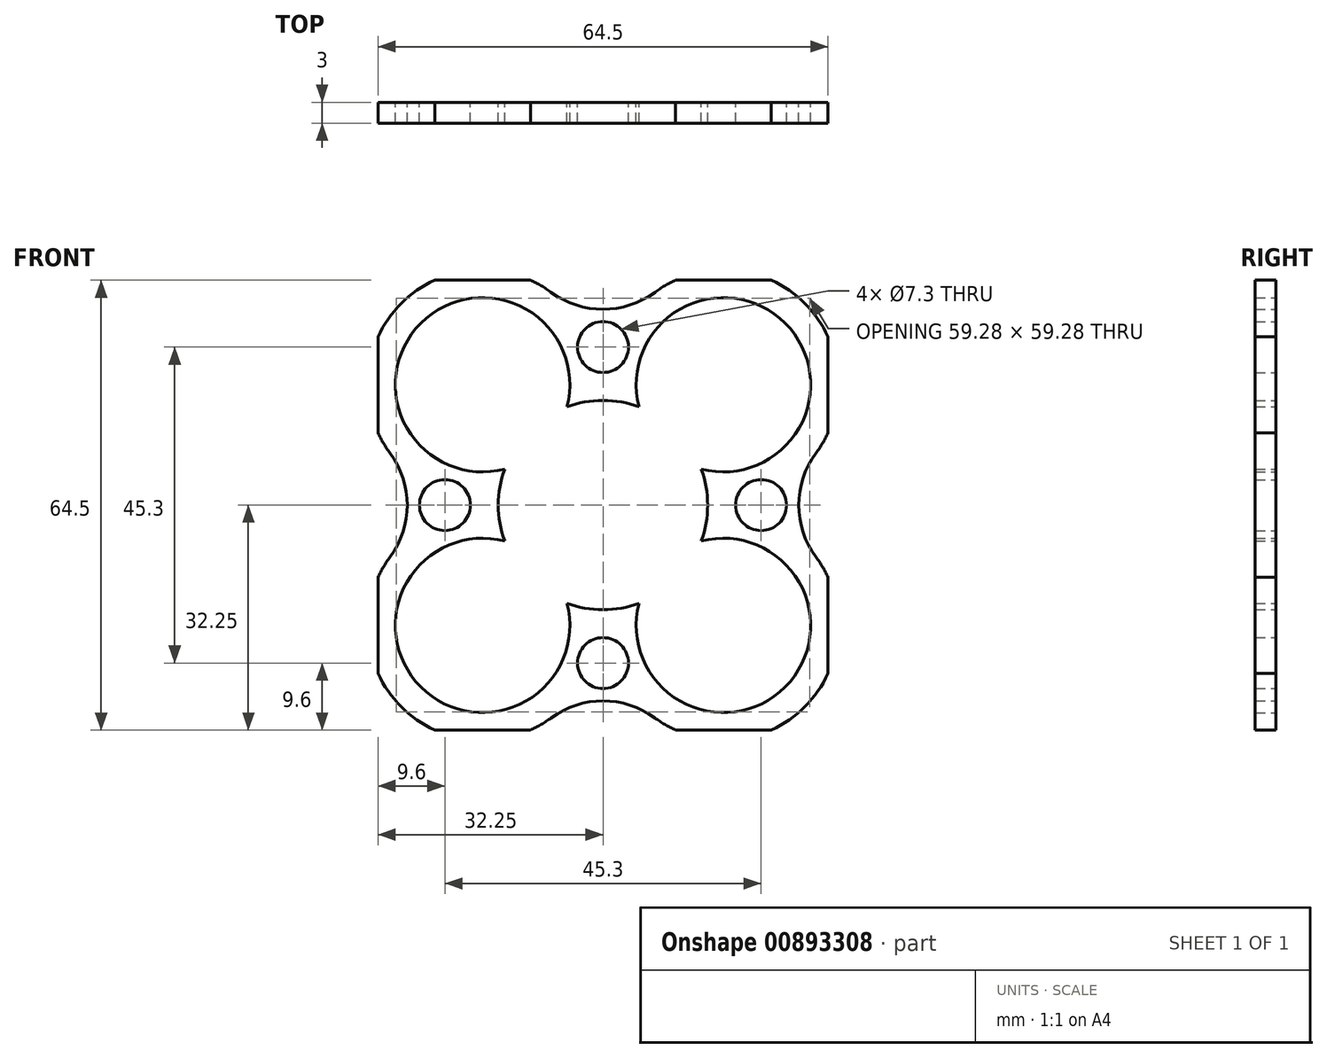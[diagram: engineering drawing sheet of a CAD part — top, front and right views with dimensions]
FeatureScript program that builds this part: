
annotation { "Feature Type Name" : "Feature", "Feature Type Description" : "" }
export const myFeature = defineFeature(function(context is Context, id is Id, definition is map)
    precondition{}
    {
        {
            var Q0;
            Q0=qCreatedBy(makeId("Front.planeOp"),FACE);
            var sketch = newSketch(context, id + "F0", { "sketchPlane" : qUnion([Q0])});
            skArc(sketch, "E0", {"start": v(5.16, 14.09) * mm, "mid": v(0, 15) * mm, "end": v(-5.16, 14.09) * mm});
            skArc(sketch, "E1", {"start": v(-5.16, 14.09) * mm, "mid": v(-26.09, 26.09) * mm, "end": v(-14.09, 5.16) * mm});
            skArc(sketch, "E2", {"start": v(14.09, 5.16) * mm, "mid": v(26.09, 26.09) * mm, "end": v(5.16, 14.09) * mm});
            skArc(sketch, "E3", {"start": v(5.16, -14.09) * mm, "mid": v(26.09, -26.09) * mm, "end": v(14.09, -5.16) * mm});
            skArc(sketch, "E4", {"start": v(-14.09, -5.16) * mm, "mid": v(-26.09, -26.09) * mm, "end": v(-5.16, -14.09) * mm});
            skArc(sketch, "E5", {"start": v(-7.44, 30.51) * mm, "mid": v(-8.86, 31.46) * mm, "end": v(-10.38, 32.25) * mm});
            skArc(sketch, "E6", {"start": v(30.51, 7.44) * mm, "mid": v(31.46, 8.86) * mm, "end": v(32.25, 10.38) * mm});
            skArc(sketch, "E7", {"start": v(7.44, -30.51) * mm, "mid": v(8.86, -31.46) * mm, "end": v(10.38, -32.25) * mm});
            skArc(sketch, "E8", {"start": v(-30.51, -7.44) * mm, "mid": v(-31.46, -8.86) * mm, "end": v(-32.25, -10.38) * mm});
            skArc(sketch, "E9.filletArc", {"start": v(-7.44, 30.51) * mm, "mid": v(0, 28.06) * mm, "end": v(7.44, 30.51) * mm});
            skArc(sketch, "E10.filletArc", {"start": v(30.51, 7.44) * mm, "mid": v(28.06, 0) * mm, "end": v(30.51, -7.44) * mm});
            skArc(sketch, "E11.filletArc", {"start": v(7.44, -30.51) * mm, "mid": v(0, -28.06) * mm, "end": v(-7.44, -30.51) * mm});
            skArc(sketch, "E12.filletArc", {"start": v(-30.51, -7.44) * mm, "mid": v(-28.06, 0) * mm, "end": v(-30.51, 7.44) * mm});
            skLineSegment(sketch, "E13", {"start": v(-24.12, 32.25) * mm, "end": v(-10.38, 32.25) * mm});
            skLineSegment(sketch, "E14.trimOffspring", {"start": v(-24.12, -32.25) * mm, "end": v(-10.38, -32.25) * mm});
            skArc(sketch, "E15.trimOffspring", {"start": v(-10.38, -32.25) * mm, "mid": v(-8.86, -31.46) * mm, "end": v(-7.44, -30.51) * mm});
            skArc(sketch, "E16.trimOffspring", {"start": v(24.12, -32.25) * mm, "mid": v(28.92, -28.92) * mm, "end": v(32.25, -24.12) * mm});
            skLineSegment(sketch, "E17.trimOffspring", {"start": v(10.38, -32.25) * mm, "end": v(24.12, -32.25) * mm});
            skLineSegment(sketch, "E18.trimOffspring", {"start": v(32.25, -24.12) * mm, "end": v(32.25, -10.38) * mm});
            skArc(sketch, "E19.trimOffspring", {"start": v(32.25, -10.38) * mm, "mid": v(31.46, -8.86) * mm, "end": v(30.51, -7.44) * mm});
            skArc(sketch, "E20.trimOffspring", {"start": v(32.25, 24.12) * mm, "mid": v(28.92, 28.92) * mm, "end": v(24.12, 32.25) * mm});
            skLineSegment(sketch, "E21.trimOffspring", {"start": v(32.25, 10.38) * mm, "end": v(32.25, 24.12) * mm});
            skLineSegment(sketch, "E22.trimOffspring", {"start": v(-32.25, -10.38) * mm, "end": v(-32.25, -24.12) * mm});
            skArc(sketch, "E23.trimOffspring", {"start": v(-32.25, 10.38) * mm, "mid": v(-31.46, 8.86) * mm, "end": v(-30.51, 7.44) * mm});
            skLineSegment(sketch, "E24.trimOffspring", {"start": v(-32.25, 24.12) * mm, "end": v(-32.25, 10.38) * mm});
            skArc(sketch, "E25.trimOffspring", {"start": v(-24.12, 32.25) * mm, "mid": v(-28.92, 28.92) * mm, "end": v(-32.25, 24.12) * mm});
            skLineSegment(sketch, "E26.trimOffspring", {"start": v(10.38, 32.25) * mm, "end": v(24.12, 32.25) * mm});
            skArc(sketch, "E27.trimOffspring", {"start": v(10.38, 32.25) * mm, "mid": v(8.86, 31.46) * mm, "end": v(7.44, 30.51) * mm});
            skArc(sketch, "E28.trimOffspring", {"start": v(-32.25, -24.12) * mm, "mid": v(-28.92, -28.92) * mm, "end": v(-24.12, -32.25) * mm});
            skPoint(sketch, "E29.center.orphan", {"position": v(-18.19, 0) * mm});
            skArc(sketch, "E30.trimOffspring", {"start": v(-14.09, 5.16) * mm, "mid": v(-15, 0) * mm, "end": v(-14.09, -5.16) * mm});
            skArc(sketch, "E31.trimOffspring", {"start": v(-5.16, -14.09) * mm, "mid": v(0, -15) * mm, "end": v(5.16, -14.09) * mm});
            skArc(sketch, "E32.trimOffspring", {"start": v(14.09, -5.16) * mm, "mid": v(15, 0) * mm, "end": v(14.09, 5.16) * mm});
            skCircle(sketch, "E33", {"center": v(0, 22.65) * mm, "radius": 3.65 * mm});
            skCircle(sketch, "E34", {"center": v(-22.65, 0) * mm, "radius": 3.65 * mm});
            skCircle(sketch, "E35", {"center": v(22.65, 0) * mm, "radius": 3.65 * mm});
            skCircle(sketch, "E36", {"center": v(0, -22.65) * mm, "radius": 3.65 * mm});
            skSolve(sketch);
        }
        {
            var Q0;
            Q0=makeQuery(id+"F0.imprint","IMPRINT",FACE,{"disambiguationData":[TD([[makeQuery(id+"F0.imprint","IMPRINT",EDGE,{"derivedFrom":sQuery(id+"F0.wireOp",EDGE,"E0")}),-1.0]])]});
            extrude(context, id + "F1", {"entities" : qUnion([Q0]), "depth" : 3 * mm, "offsetDistance" : 25 * mm});
        }
    });
